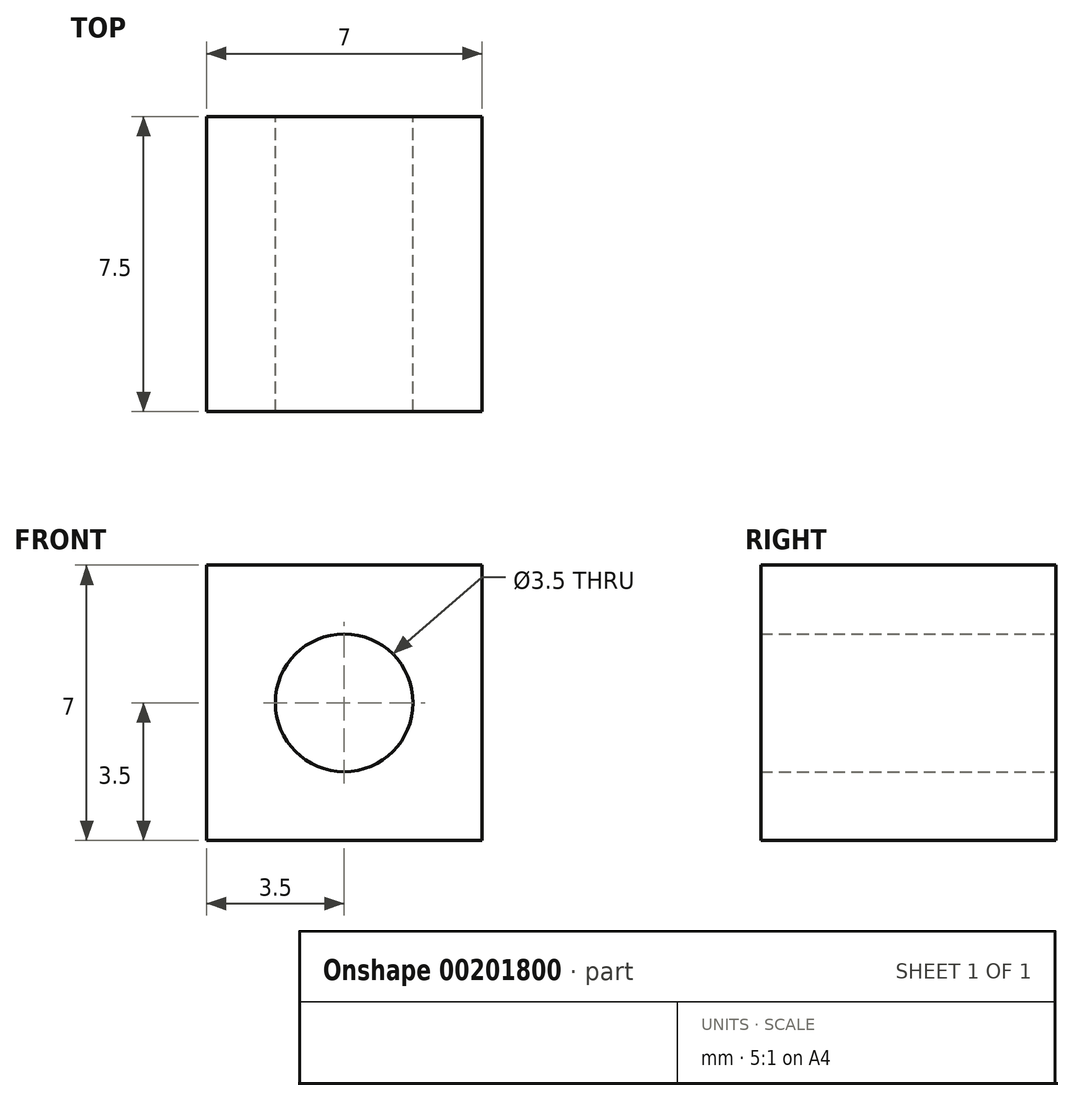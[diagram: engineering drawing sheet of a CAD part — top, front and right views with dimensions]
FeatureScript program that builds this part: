
annotation { "Feature Type Name" : "Feature", "Feature Type Description" : "" }
export const myFeature = defineFeature(function(context is Context, id is Id, definition is map)
    precondition{}
    {
        {
            var Q0;
            Q0=qCreatedBy(makeId("Front.planeOp"),FACE);
            var sketch = newSketch(context, id + "F0", { "sketchPlane" : qUnion([Q0])});
            skCircle(sketch, "E0", {"center": v(0, 0) * mm, "radius": 1.75 * mm});
            skLineSegment(sketch, "E1.bottom", {"start": v(3.5, 3.5) * mm, "end": v(-3.5, 3.5) * mm});
            skLineSegment(sketch, "E1.top", {"start": v(3.5, -3.5) * mm, "end": v(-3.5, -3.5) * mm});
            skLineSegment(sketch, "E1.left", {"start": v(3.5, 3.5) * mm, "end": v(3.5, -3.5) * mm});
            skLineSegment(sketch, "E1.right", {"start": v(-3.5, 3.5) * mm, "end": v(-3.5, -3.5) * mm});
            skSolve(sketch);
        }
        {
            var Q0;
            Q0 = qSketchRegion(id + "F0", true);
            extrude(context, id + "F1", {"entities" : qUnion([Q0]), "depth" : 7.5 * mm});
        }
    });
